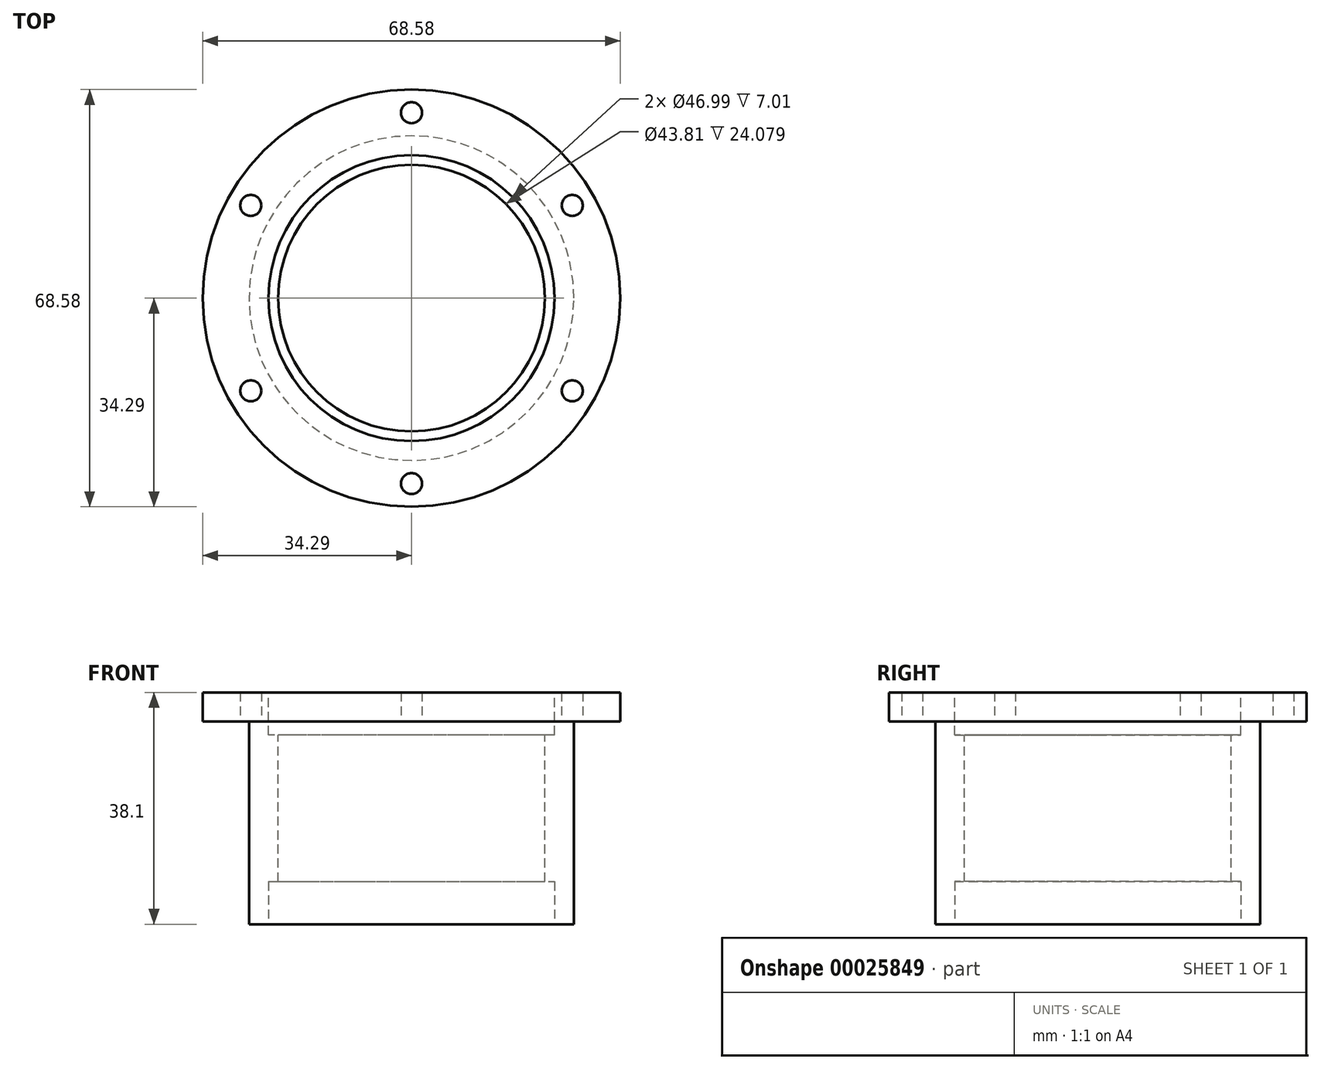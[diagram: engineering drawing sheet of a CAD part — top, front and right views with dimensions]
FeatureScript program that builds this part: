
annotation { "Feature Type Name" : "Feature", "Feature Type Description" : "" }
export const myFeature = defineFeature(function(context is Context, id is Id, definition is map)
    precondition{}
    {
        {
            var Q0;
            Q0=qCreatedBy(makeId("Front.planeOp"),FACE);
            var sketch = newSketch(context, id + "F0", { "sketchPlane" : qUnion([Q0])});
            skLineSegment(sketch, "E0", {"start": v(0, 0) * mm, "end": v(0, 38.1) * mm});
            skLineSegment(sketch, "E1", {"start": v(0, 38.1) * mm, "end": v(34.3, 38.1) * mm});
            skLineSegment(sketch, "E2", {"start": v(34.3, 38.1) * mm, "end": v(34.3, 33.32) * mm});
            skLineSegment(sketch, "E3", {"start": v(34.3, 33.32) * mm, "end": v(26.67, 33.32) * mm});
            skLineSegment(sketch, "E4", {"start": v(26.67, 33.32) * mm, "end": v(26.67, 0) * mm});
            skLineSegment(sketch, "E5", {"start": v(26.67, 0) * mm, "end": v(0, 0) * mm});
            skSolve(sketch);
        }
        {
            var Q0;
            Q0 = qSketchRegion(id + "F0", true);
            var Q1;
            Q1=sQuery(id+"F0.wireOp",EDGE,"E0");
            revolve(context, id + "F1", {"entities" : qUnion([Q0]), "axis" : qUnion([Q1]), "revolveType" : RevolveType.FULL});
        }
        {
            var Q0;
            Q0=makeQuery(id+"F1.opRevolve","SWEPT_FACE",FACE,{"disambiguationData":[OSD([sQuery(id+"F0.wireOp",EDGE,"E3")])]});
            var sketch = newSketch(context, id + "F2", { "sketchPlane" : qUnion([Q0])});
            skLineSegment(sketch, "E6", {"start": v(-69.16, 0) * mm, "end": v(68.2, 0) * mm, "construction": true});
            skLineSegment(sketch, "E7", {"start": v(0, 54.12) * mm, "end": v(0, -51.4) * mm, "construction": true});
            skCircle(sketch, "E8", {"center": v(-0.49, 0) * mm, "radius": 30.48 * mm});
            skCircle(sketch, "E9.cCircle", {"center": v(0, 0) * mm, "radius": 30.48 * mm, "construction": true});
            skLineSegment(sketch, "E9.0", {"start": v(0, -30.48) * mm, "end": v(-26.4, -15.24) * mm});
            skLineSegment(sketch, "E9.1", {"start": v(-26.4, -15.24) * mm, "end": v(-26.4, 15.24) * mm});
            skLineSegment(sketch, "E9.2", {"start": v(-26.4, 15.24) * mm, "end": v(0, 30.48) * mm});
            skLineSegment(sketch, "E9.3", {"start": v(0, 30.48) * mm, "end": v(26.4, 15.24) * mm});
            skLineSegment(sketch, "E9.4", {"start": v(26.4, 15.24) * mm, "end": v(26.4, -15.24) * mm});
            skLineSegment(sketch, "E9.5", {"start": v(26.4, -15.24) * mm, "end": v(0, -30.48) * mm});
            skPoint(sketch, "E10", {"position": v(-26.4, -15.24) * mm});
            skPoint(sketch, "E11", {"position": v(-26.4, 15.24) * mm});
            skPoint(sketch, "E12", {"position": v(0, 30.48) * mm});
            skPoint(sketch, "E13", {"position": v(26.4, 15.24) * mm});
            skPoint(sketch, "E14", {"position": v(26.4, -15.24) * mm});
            skPoint(sketch, "E15", {"position": v(0, -30.48) * mm});
            skSolve(sketch);
        }
        {
            var Q0;
            Q0=sQuery(id+"F2.wireOp",VERTEX,"E10");
            var Q1;
            Q1=sQuery(id+"F2.wireOp",VERTEX,"E11");
            var Q2;
            Q2=sQuery(id+"F2.wireOp",VERTEX,"E12");
            var Q3;
            Q3=sQuery(id+"F2.wireOp",VERTEX,"E13");
            var Q4;
            Q4=sQuery(id+"F2.wireOp",VERTEX,"E14");
            var Q5;
            Q5=sQuery(id+"F2.wireOp",VERTEX,"E15");
            var Q6;
            Q6=makeQuery(id+"F1.opRevolve","SWEPT_BODY",BODY,{"disambiguationData":[OSD([sQuery(id+"F0.wireOp",EDGE,"E0"),sQuery(id+"F0.wireOp",EDGE,"E1"),sQuery(id+"F0.wireOp",EDGE,"E2"),sQuery(id+"F0.wireOp",EDGE,"E3"),sQuery(id+"F0.wireOp",EDGE,"E4"),sQuery(id+"F0.wireOp",EDGE,"E5")])]});
            hole(context, id + "F3", {"style" : HoleStyle.SIMPLE, "holeDiameter" : 3.45 * mm, "endStyle" : HoleEndStyle.THROUGH, "locations" : qUnion([Q0, Q1, Q2, Q3, Q4, Q5]), "scope" : qUnion([Q6])});
        }
        {
            var Q0;
            Q0=makeQuery(id+"F1.opRevolve","SWEPT_FACE",FACE,{"disambiguationData":[OSD([sQuery(id+"F0.wireOp",EDGE,"E1")])]});
            var sketch = newSketch(context, id + "F4", { "sketchPlane" : qUnion([Q0])});
            skCircle(sketch, "E16", {"center": v(0, 0) * mm, "radius": 21.9 * mm});
            skSolve(sketch);
        }
        {
            var Q0;
            Q0 = qSketchRegion(id + "F4", true);
            extrude(context, id + "F5", {"entities" : qUnion([Q0]), "operationType" : NewBodyOperationType.REMOVE, "oppositeDirection" : true, "depth" : 57.57 * mm});
        }
        {
            var Q0;
            Q0=makeQuery(id+"F1.opRevolve","SWEPT_FACE",FACE,{"disambiguationData":[OSD([sQuery(id+"F0.wireOp",EDGE,"E1")])]});
            var sketch = newSketch(context, id + "F6", { "sketchPlane" : qUnion([Q0])});
            skCircle(sketch, "E17", {"center": v(0, 0) * mm, "radius": 23.5 * mm});
            skSolve(sketch);
        }
        {
            var Q0;
            Q0 = qSketchRegion(id + "F6", true);
            extrude(context, id + "F7", {"entities" : qUnion([Q0]), "operationType" : NewBodyOperationType.REMOVE, "oppositeDirection" : true, "depth" : 7 * mm});
        }
        {
            var Q0;
            Q0=makeQuery(id+"F1.opRevolve","SWEPT_FACE",FACE,{"disambiguationData":[OSD([sQuery(id+"F0.wireOp",EDGE,"E5")])]});
            var sketch = newSketch(context, id + "F8", { "sketchPlane" : qUnion([Q0])});
            skCircle(sketch, "E18", {"center": v(0, 0) * mm, "radius": 23.5 * mm});
            skSolve(sketch);
        }
        {
            var Q0;
            Q0 = qSketchRegion(id + "F8", true);
            extrude(context, id + "F9", {"entities" : qUnion([Q0]), "operationType" : NewBodyOperationType.REMOVE, "oppositeDirection" : true, "depth" : 7 * mm});
        }
    });
